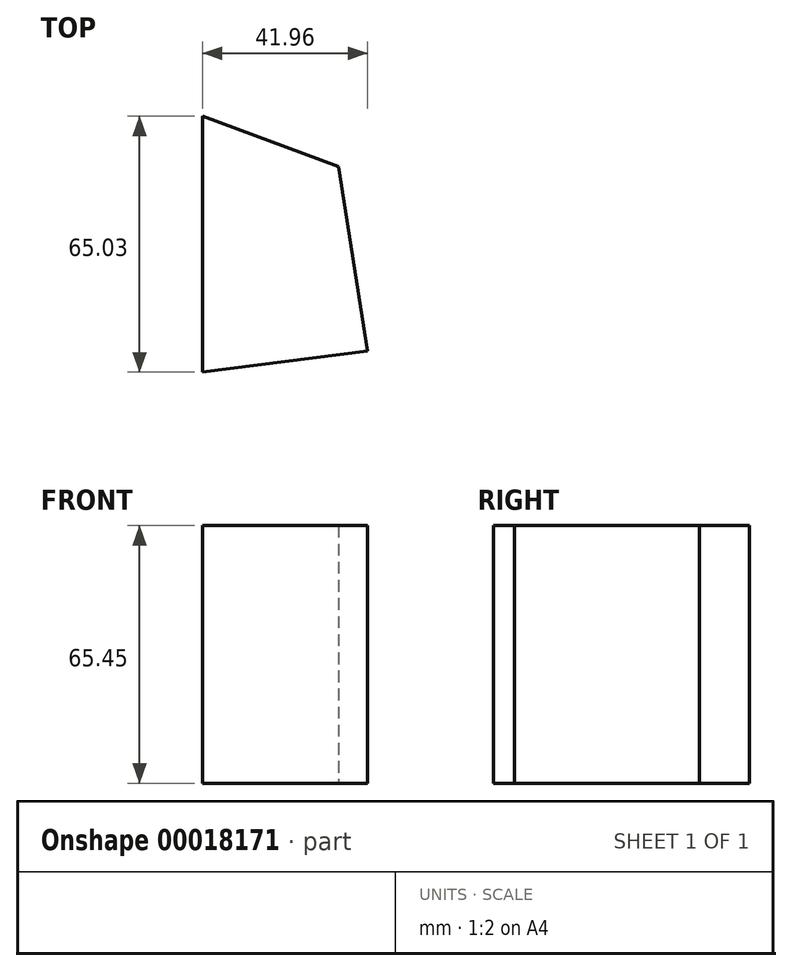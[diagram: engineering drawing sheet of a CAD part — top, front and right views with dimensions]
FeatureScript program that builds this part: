
annotation { "Feature Type Name" : "Feature", "Feature Type Description" : "" }
export const myFeature = defineFeature(function(context is Context, id is Id, definition is map)
    precondition{}
    {
        {
            var Q0;
            Q0=qCreatedBy(makeId("Top.planeOp"),FACE);
            var sketch = newSketch(context, id + "F0", { "sketchPlane" : qUnion([Q0])});
            skLineSegment(sketch, "E0", {"start": v(-41.96, 39) * mm, "end": v(-41.96, -26.03) * mm});
            skLineSegment(sketch, "E1", {"start": v(-41.96, -26.03) * mm, "end": v(0, -20.7) * mm});
            skLineSegment(sketch, "E2", {"start": v(0, -20.7) * mm, "end": v(-7.44, 26.22) * mm});
            skLineSegment(sketch, "E3", {"start": v(-7.44, 26.22) * mm, "end": v(-41.96, 39) * mm});
            skSolve(sketch);
        }
        {
            var Q0;
            Q0=makeQuery(id+"F0.imprint","IMPRINT",FACE,{"disambiguationData":[TD([[makeQuery(id+"F0.imprint","IMPRINT",EDGE,{"derivedFrom":sQuery(id+"F0.wireOp",EDGE,"E0")}),1.0]])]});
            extrude(context, id + "F1", {"entities" : qUnion([Q0]), "depth" : 65.45 * mm});
        }
    });
